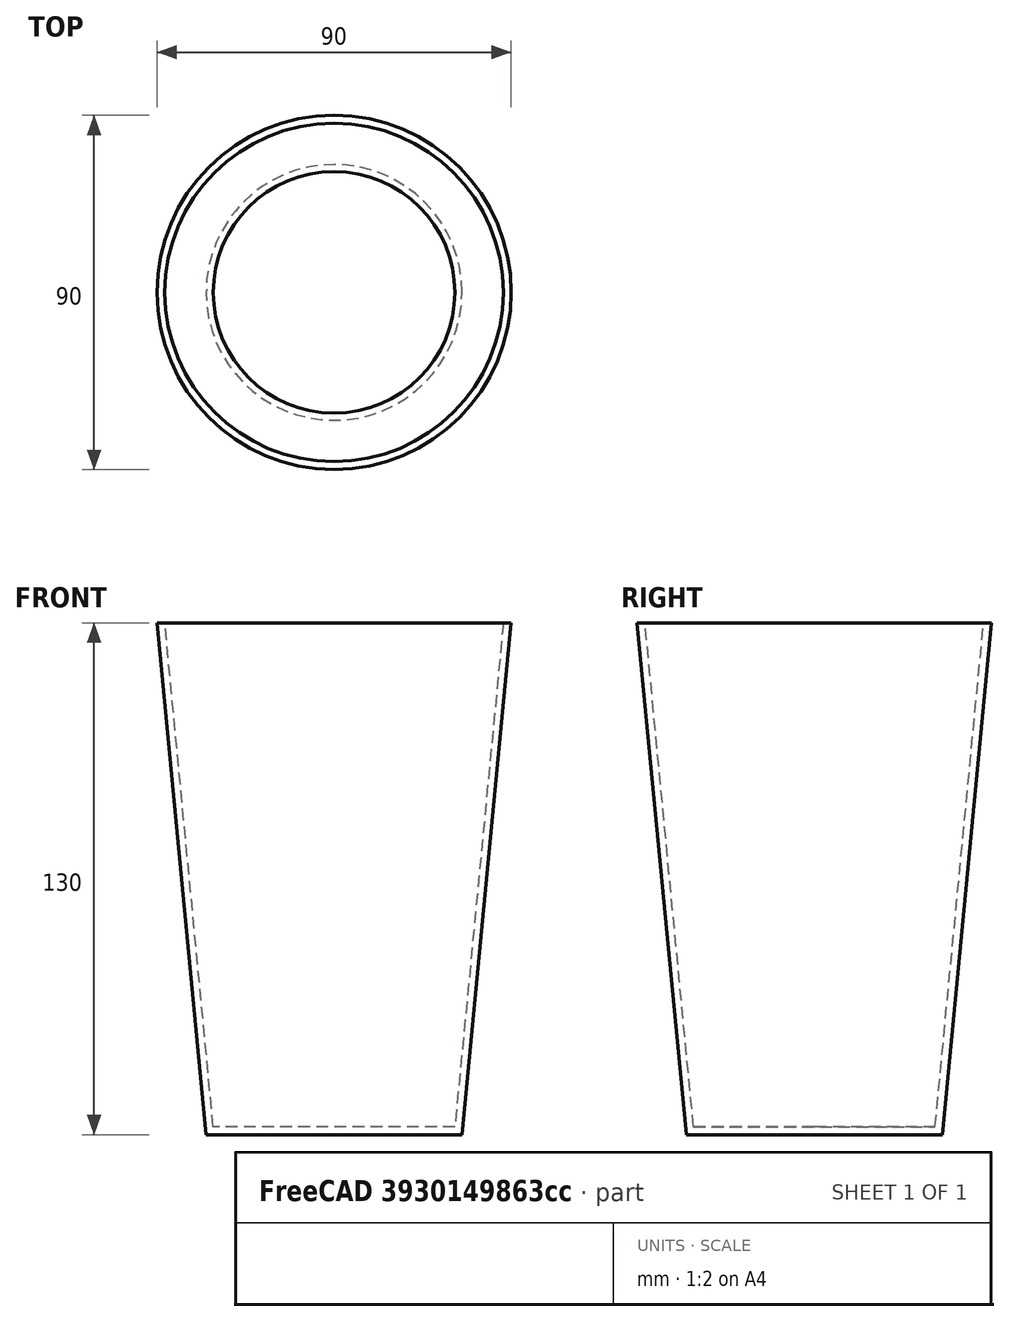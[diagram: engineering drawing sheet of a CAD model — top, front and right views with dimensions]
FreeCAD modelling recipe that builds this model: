
FCSTD DOCUMENT  (FreeCAD 0.19R24267 +148 (Git))
Label: Cub
License: All rights reserved
LicenseURL: http://en.wikipedia.org/wiki/All_rights_reserved
objects: Sketcher::SketchObject×1, PartDesign::Revolution×1, PartDesign::Body×1
note: 4 computed .brp shape members not serialized (recipe doc carries the construction recipe); baked Part::Feature solids carry a one-line shape summary decoded from their .brp

FEATURE [Sketcher::SketchObject] Sketch
  FullyConstrained = true
  MapMode = 5
  Placement = pos=(0,0,0) rot=(1,0,0;1.5708rad)
  Support = -> [XZ_Plane]
  sketch-geometry (6):
    g0: LineSegment StartX=0 StartY=0 StartZ=0 EndX=32.5 EndY=0 EndZ=0
    g1: LineSegment StartX=32.5 StartY=0 StartZ=0 EndX=45 EndY=130 EndZ=0
    g2: LineSegment StartX=43 StartY=130 StartZ=0 EndX=30.6923 EndY=2 EndZ=0
    g3: LineSegment StartX=30.6923 StartY=2 StartZ=0 EndX=0 EndY=2 EndZ=0
    g4: LineSegment StartX=0 StartY=2 StartZ=0 EndX=0 EndY=0 EndZ=0
    g5: LineSegment StartX=43 StartY=130 StartZ=0 EndX=45 EndY=130 EndZ=0
  constraints (17):
    c: Coincident(g0,g-1)
    c: Horizontal(g0)
    c: Coincident(g1,g0)
    c: Coincident(g3,g2)
    c: Horizontal(g3)
    c: Coincident(g4,g3)
    c: Vertical(g4)
    c: Coincident(g4,g0)
    c: Parallel(g2,g1)
    c: DistanceY(g4,g4) = 2
    c: DistanceX(g0,g0) = 32.5
    c: DistanceY(g0,g2) = 130
    c: DistanceX(g3,g1) = 45
    c: Coincident(g5,g2)
    c: Coincident(g5,g1)
    c: Horizontal(g5)
    c: Equal(g5,g4)
FEATURE [PartDesign::Revolution] Revolution
  Angle = 360
  Axis = (0,-2e-16,1)
  Base = (0,0,0)
  Placement = pos=(0,0,0) rot=(1,0,0;1.5708rad)
  Profile = -> Sketch
  ReferenceAxis = -> Sketch [V_Axis]
  Reversed = true
FEATURE [PartDesign::Body] Body
  Group = -> [Sketch,Revolution]
  Origin = -> Origin
  Tip = -> Revolution
